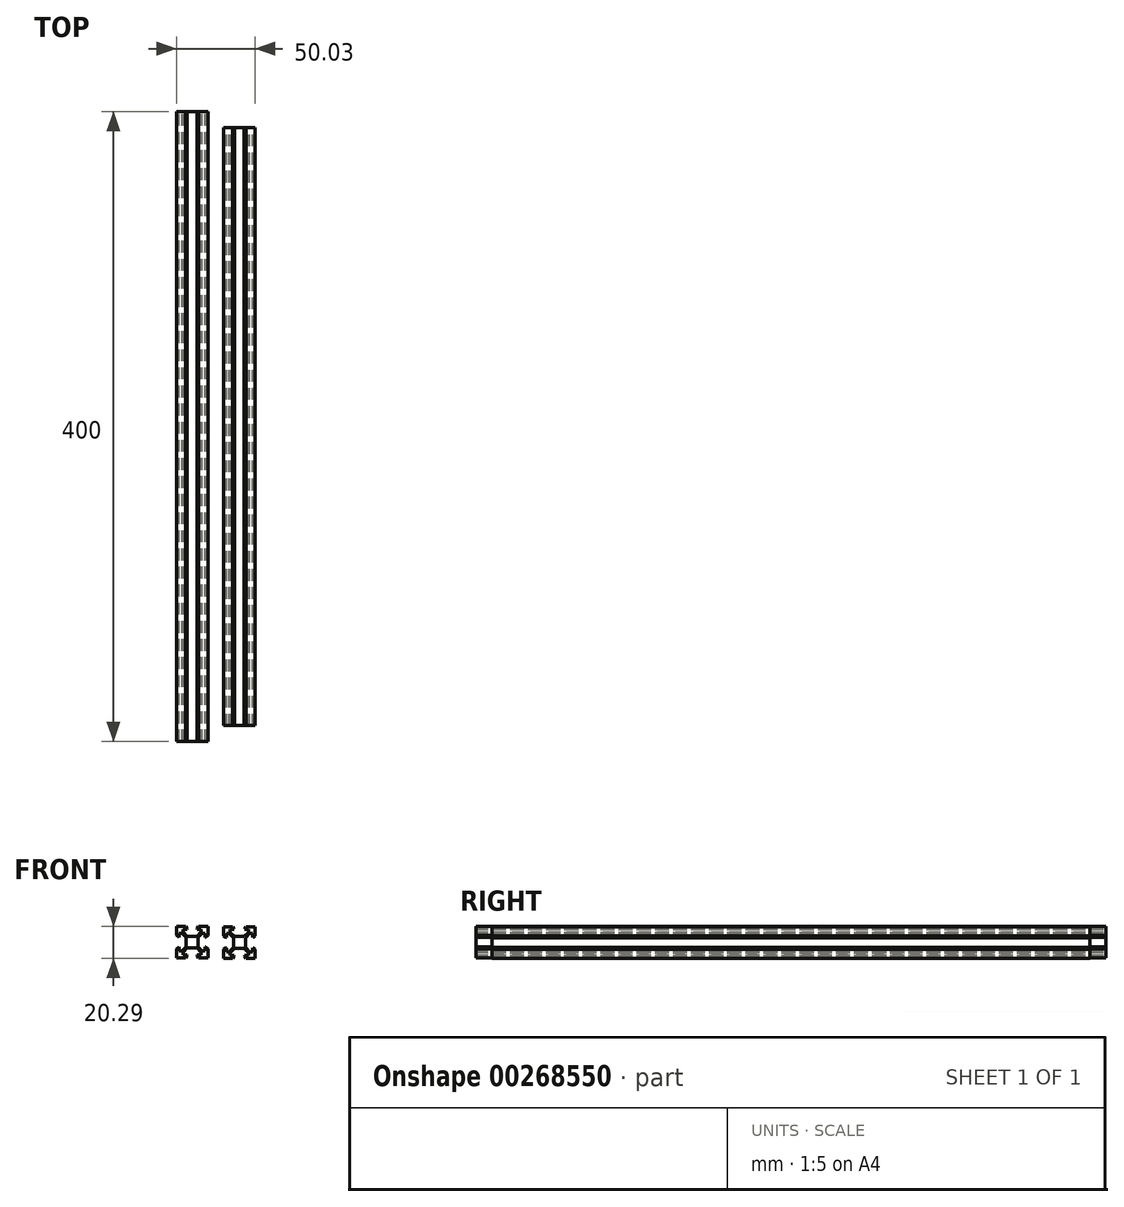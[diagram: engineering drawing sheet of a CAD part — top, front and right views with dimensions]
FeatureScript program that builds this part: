
annotation { "Feature Type Name" : "Feature", "Feature Type Description" : "" }
export const myFeature = defineFeature(function(context is Context, id is Id, definition is map)
    precondition{}
    {
        {
            var Q0;
            Q0=qCreatedBy(makeId("Front.planeOp"),FACE);
            var sketch = newSketch(context, id + "F0", { "sketchPlane" : qUnion([Q0])});
            skLineSegment(sketch, "E0.bottom", {"start": v(10, -10) * mm, "end": v(-10, -10) * mm});
            skLineSegment(sketch, "E0.top", {"start": v(10, 10) * mm, "end": v(-10, 10) * mm});
            skLineSegment(sketch, "E0.left", {"start": v(10, -10) * mm, "end": v(10, 10) * mm});
            skLineSegment(sketch, "E0.right", {"start": v(-10, -10) * mm, "end": v(-10, 10) * mm});
            skPoint(sketch, "E0.middle", {"position": v(0, 0) * mm});
            skLineSegment(sketch, "E1", {"start": v(4.24, 10) * mm, "end": v(3.26, 8.42) * mm});
            skLineSegment(sketch, "E2", {"start": v(3.26, 8.42) * mm, "end": v(3.26, 8.22) * mm});
            skLineSegment(sketch, "E3", {"start": v(3.26, 8.22) * mm, "end": v(5.76, 8.22) * mm});
            skLineSegment(sketch, "E4", {"start": v(5.76, 8.22) * mm, "end": v(5.76, 6.44) * mm});
            skLineSegment(sketch, "E5", {"start": v(5.76, 6.44) * mm, "end": v(3.11, 3.78) * mm});
            skLineSegment(sketch, "E6", {"start": v(3.11, 3.78) * mm, "end": v(0, 3.78) * mm});
            skLineSegment(sketch, "E7", {"start": v(0, 15.87) * mm, "end": v(0, -18.37) * mm, "construction": true});
            skPoint(sketch, "E7.endSnap0", {"position": v(0, -10) * mm});
            skLineSegment(sketch, "E8.MirrorCS", {"start": v(-4.24, 10) * mm, "end": v(-3.26, 8.42) * mm});
            skLineSegment(sketch, "E9.MirrorCS", {"start": v(-3.26, 8.42) * mm, "end": v(-3.26, 8.22) * mm});
            skLineSegment(sketch, "E10.MirrorCS", {"start": v(-3.26, 8.22) * mm, "end": v(-5.76, 8.22) * mm});
            skLineSegment(sketch, "E11.MirrorCS", {"start": v(-5.46, 15.87) * mm, "end": v(-5.46, -18.37) * mm, "construction": true});
            skLineSegment(sketch, "E12.MirrorCS", {"start": v(-5.76, 6.44) * mm, "end": v(-3.11, 3.78) * mm});
            skLineSegment(sketch, "E13.MirrorCS", {"start": v(-3.11, 3.78) * mm, "end": v(0, 3.78) * mm});
            skLineSegment(sketch, "E14.MirrorCS", {"start": v(-5.76, 8.22) * mm, "end": v(-5.76, 6.44) * mm});
            skLineSegment(sketch, "E15.1.0", {"start": v(-3.78, 3.11) * mm, "end": v(-3.78, 0) * mm});
            skLineSegment(sketch, "E15.1.1", {"start": v(-3.78, -3.11) * mm, "end": v(-3.78, 0) * mm});
            skLineSegment(sketch, "E15.1.2", {"start": v(-6.44, -5.76) * mm, "end": v(-3.78, -3.11) * mm});
            skLineSegment(sketch, "E15.1.3", {"start": v(-8.22, 3.26) * mm, "end": v(-8.22, 5.76) * mm});
            skLineSegment(sketch, "E15.1.4", {"start": v(-10, 4.24) * mm, "end": v(-8.42, 3.26) * mm});
            skLineSegment(sketch, "E15.1.5", {"start": v(-8.22, 5.76) * mm, "end": v(-6.44, 5.76) * mm});
            skLineSegment(sketch, "E15.1.6", {"start": v(-10, -4.24) * mm, "end": v(-8.42, -3.26) * mm});
            skLineSegment(sketch, "E15.1.7", {"start": v(-6.44, 5.76) * mm, "end": v(-3.78, 3.11) * mm});
            skLineSegment(sketch, "E15.1.8", {"start": v(-8.22, -5.76) * mm, "end": v(-6.44, -5.76) * mm});
            skLineSegment(sketch, "E15.1.9", {"start": v(-8.22, -3.26) * mm, "end": v(-8.22, -5.76) * mm});
            skLineSegment(sketch, "E15.1.10", {"start": v(-8.42, -3.26) * mm, "end": v(-8.22, -3.26) * mm});
            skLineSegment(sketch, "E15.1.11", {"start": v(-8.42, 3.26) * mm, "end": v(-8.22, 3.26) * mm});
            skLineSegment(sketch, "E15.2.0", {"start": v(-3.11, -3.78) * mm, "end": v(0, -3.78) * mm});
            skLineSegment(sketch, "E15.2.1", {"start": v(3.11, -3.78) * mm, "end": v(0, -3.78) * mm});
            skLineSegment(sketch, "E15.2.2", {"start": v(5.76, -6.44) * mm, "end": v(3.11, -3.78) * mm});
            skLineSegment(sketch, "E15.2.3", {"start": v(-3.26, -8.22) * mm, "end": v(-5.76, -8.22) * mm});
            skLineSegment(sketch, "E15.2.4", {"start": v(-4.24, -10) * mm, "end": v(-3.26, -8.42) * mm});
            skLineSegment(sketch, "E15.2.5", {"start": v(-5.76, -8.22) * mm, "end": v(-5.76, -6.44) * mm});
            skLineSegment(sketch, "E15.2.6", {"start": v(4.24, -10) * mm, "end": v(3.26, -8.42) * mm});
            skLineSegment(sketch, "E15.2.7", {"start": v(-5.76, -6.44) * mm, "end": v(-3.11, -3.78) * mm});
            skLineSegment(sketch, "E15.2.8", {"start": v(5.76, -8.22) * mm, "end": v(5.76, -6.44) * mm});
            skLineSegment(sketch, "E15.2.9", {"start": v(3.26, -8.22) * mm, "end": v(5.76, -8.22) * mm});
            skLineSegment(sketch, "E15.2.10", {"start": v(3.26, -8.42) * mm, "end": v(3.26, -8.22) * mm});
            skLineSegment(sketch, "E15.2.11", {"start": v(-3.26, -8.42) * mm, "end": v(-3.26, -8.22) * mm});
            skLineSegment(sketch, "E15.3.0", {"start": v(3.78, -3.11) * mm, "end": v(3.78, 0) * mm});
            skLineSegment(sketch, "E15.3.1", {"start": v(3.78, 3.11) * mm, "end": v(3.78, 0) * mm});
            skLineSegment(sketch, "E15.3.2", {"start": v(6.44, 5.76) * mm, "end": v(3.78, 3.11) * mm});
            skLineSegment(sketch, "E15.3.3", {"start": v(8.22, -3.26) * mm, "end": v(8.22, -5.76) * mm});
            skLineSegment(sketch, "E15.3.4", {"start": v(10, -4.24) * mm, "end": v(8.42, -3.26) * mm});
            skLineSegment(sketch, "E15.3.5", {"start": v(8.22, -5.76) * mm, "end": v(6.44, -5.76) * mm});
            skLineSegment(sketch, "E15.3.6", {"start": v(10, 4.24) * mm, "end": v(8.42, 3.26) * mm});
            skLineSegment(sketch, "E15.3.7", {"start": v(6.44, -5.76) * mm, "end": v(3.78, -3.11) * mm});
            skLineSegment(sketch, "E15.3.8", {"start": v(8.22, 5.76) * mm, "end": v(6.44, 5.76) * mm});
            skLineSegment(sketch, "E15.3.9", {"start": v(8.22, 3.26) * mm, "end": v(8.22, 5.76) * mm});
            skLineSegment(sketch, "E15.3.10", {"start": v(8.42, 3.26) * mm, "end": v(8.22, 3.26) * mm});
            skLineSegment(sketch, "E15.3.11", {"start": v(8.42, -3.26) * mm, "end": v(8.22, -3.26) * mm});
            skSolve(sketch);
        }
        {
            var Q0;
            {var subQ15=sQuery(id+"F0.wireOp",EDGE,"E1");Q0=makeQuery(id+"F0.imprint","IMPRINT",FACE,{"disambiguationData":[TD([[makeQuery(id+"F0.imprint","IMPRINT",EDGE,{"derivedFrom":subQ15}),1.0]])]});}
            extrude(context, id + "F1", {"entities" : qUnion([Q0]), "endBound" : BoundingType.SYMMETRIC, "depth" : 380 * mm});
        }
        {
            var Q0;
            Q0=makeQuery(id+"F1.opExtrude","SWEPT_BODY",BODY,{"disambiguationData":[OSD([sQuery(id+"F0.wireOp",EDGE,"E0.bottom"),sQuery(id+"F0.wireOp",EDGE,"E0.top"),sQuery(id+"F0.wireOp",EDGE,"E0.left"),sQuery(id+"F0.wireOp",EDGE,"E0.right"),sQuery(id+"F0.wireOp",EDGE,"E1"),sQuery(id+"F0.wireOp",EDGE,"E2"),sQuery(id+"F0.wireOp",EDGE,"E3"),sQuery(id+"F0.wireOp",EDGE,"E4"),sQuery(id+"F0.wireOp",EDGE,"E5"),sQuery(id+"F0.wireOp",EDGE,"E6"),sQuery(id+"F0.wireOp",EDGE,"E8.MirrorCS"),sQuery(id+"F0.wireOp",EDGE,"E9.MirrorCS"),sQuery(id+"F0.wireOp",EDGE,"E10.MirrorCS"),sQuery(id+"F0.wireOp",EDGE,"E12.MirrorCS"),sQuery(id+"F0.wireOp",EDGE,"E13.MirrorCS"),sQuery(id+"F0.wireOp",EDGE,"E14.MirrorCS"),sQuery(id+"F0.wireOp",EDGE,"E15.1.0"),sQuery(id+"F0.wireOp",EDGE,"E15.1.1"),sQuery(id+"F0.wireOp",EDGE,"E15.1.2"),sQuery(id+"F0.wireOp",EDGE,"E15.1.3"),sQuery(id+"F0.wireOp",EDGE,"E15.1.4"),sQuery(id+"F0.wireOp",EDGE,"E15.1.5"),sQuery(id+"F0.wireOp",EDGE,"E15.1.6"),sQuery(id+"F0.wireOp",EDGE,"E15.1.7"),sQuery(id+"F0.wireOp",EDGE,"E15.1.8"),sQuery(id+"F0.wireOp",EDGE,"E15.1.9"),sQuery(id+"F0.wireOp",EDGE,"E15.1.10"),sQuery(id+"F0.wireOp",EDGE,"E15.1.11"),sQuery(id+"F0.wireOp",EDGE,"E15.2.0"),sQuery(id+"F0.wireOp",EDGE,"E15.2.1"),sQuery(id+"F0.wireOp",EDGE,"E15.2.2"),sQuery(id+"F0.wireOp",EDGE,"E15.2.3"),sQuery(id+"F0.wireOp",EDGE,"E15.2.4"),sQuery(id+"F0.wireOp",EDGE,"E15.2.5"),sQuery(id+"F0.wireOp",EDGE,"E15.2.6"),sQuery(id+"F0.wireOp",EDGE,"E15.2.7"),sQuery(id+"F0.wireOp",EDGE,"E15.2.8"),sQuery(id+"F0.wireOp",EDGE,"E15.2.9"),sQuery(id+"F0.wireOp",EDGE,"E15.2.10"),sQuery(id+"F0.wireOp",EDGE,"E15.2.11"),sQuery(id+"F0.wireOp",EDGE,"E15.3.0"),sQuery(id+"F0.wireOp",EDGE,"E15.3.1"),sQuery(id+"F0.wireOp",EDGE,"E15.3.2"),sQuery(id+"F0.wireOp",EDGE,"E15.3.3"),sQuery(id+"F0.wireOp",EDGE,"E15.3.4"),sQuery(id+"F0.wireOp",EDGE,"E15.3.5"),sQuery(id+"F0.wireOp",EDGE,"E15.3.6"),sQuery(id+"F0.wireOp",EDGE,"E15.3.7"),sQuery(id+"F0.wireOp",EDGE,"E15.3.8"),sQuery(id+"F0.wireOp",EDGE,"E15.3.9"),sQuery(id+"F0.wireOp",EDGE,"E15.3.10"),sQuery(id+"F0.wireOp",EDGE,"E15.3.11")])]});
            transform(context, id + "F2", {"entities" : qUnion([Q0]), "transformType" : TransformType.COPY});
        }
        {
            var Q0;
            Q0=makeQuery(id+"F2.opPattern","COPY",BODY,{"derivedFrom":makeQuery(id+"F1.opExtrude","SWEPT_BODY",BODY,{"disambiguationData":[OSD([sQuery(id+"F0.wireOp",EDGE,"E0.bottom"),sQuery(id+"F0.wireOp",EDGE,"E0.top"),sQuery(id+"F0.wireOp",EDGE,"E0.left"),sQuery(id+"F0.wireOp",EDGE,"E0.right"),sQuery(id+"F0.wireOp",EDGE,"E1"),sQuery(id+"F0.wireOp",EDGE,"E2"),sQuery(id+"F0.wireOp",EDGE,"E3"),sQuery(id+"F0.wireOp",EDGE,"E4"),sQuery(id+"F0.wireOp",EDGE,"E5"),sQuery(id+"F0.wireOp",EDGE,"E6"),sQuery(id+"F0.wireOp",EDGE,"E8.MirrorCS"),sQuery(id+"F0.wireOp",EDGE,"E9.MirrorCS"),sQuery(id+"F0.wireOp",EDGE,"E10.MirrorCS"),sQuery(id+"F0.wireOp",EDGE,"E12.MirrorCS"),sQuery(id+"F0.wireOp",EDGE,"E13.MirrorCS"),sQuery(id+"F0.wireOp",EDGE,"E14.MirrorCS"),sQuery(id+"F0.wireOp",EDGE,"E15.1.0"),sQuery(id+"F0.wireOp",EDGE,"E15.1.1"),sQuery(id+"F0.wireOp",EDGE,"E15.1.2"),sQuery(id+"F0.wireOp",EDGE,"E15.1.3"),sQuery(id+"F0.wireOp",EDGE,"E15.1.4"),sQuery(id+"F0.wireOp",EDGE,"E15.1.5"),sQuery(id+"F0.wireOp",EDGE,"E15.1.6"),sQuery(id+"F0.wireOp",EDGE,"E15.1.7"),sQuery(id+"F0.wireOp",EDGE,"E15.1.8"),sQuery(id+"F0.wireOp",EDGE,"E15.1.9"),sQuery(id+"F0.wireOp",EDGE,"E15.1.10"),sQuery(id+"F0.wireOp",EDGE,"E15.1.11"),sQuery(id+"F0.wireOp",EDGE,"E15.2.0"),sQuery(id+"F0.wireOp",EDGE,"E15.2.1"),sQuery(id+"F0.wireOp",EDGE,"E15.2.2"),sQuery(id+"F0.wireOp",EDGE,"E15.2.3"),sQuery(id+"F0.wireOp",EDGE,"E15.2.4"),sQuery(id+"F0.wireOp",EDGE,"E15.2.5"),sQuery(id+"F0.wireOp",EDGE,"E15.2.6"),sQuery(id+"F0.wireOp",EDGE,"E15.2.7"),sQuery(id+"F0.wireOp",EDGE,"E15.2.8"),sQuery(id+"F0.wireOp",EDGE,"E15.2.9"),sQuery(id+"F0.wireOp",EDGE,"E15.2.10"),sQuery(id+"F0.wireOp",EDGE,"E15.2.11"),sQuery(id+"F0.wireOp",EDGE,"E15.3.0"),sQuery(id+"F0.wireOp",EDGE,"E15.3.1"),sQuery(id+"F0.wireOp",EDGE,"E15.3.2"),sQuery(id+"F0.wireOp",EDGE,"E15.3.3"),sQuery(id+"F0.wireOp",EDGE,"E15.3.4"),sQuery(id+"F0.wireOp",EDGE,"E15.3.5"),sQuery(id+"F0.wireOp",EDGE,"E15.3.6"),sQuery(id+"F0.wireOp",EDGE,"E15.3.7"),sQuery(id+"F0.wireOp",EDGE,"E15.3.8"),sQuery(id+"F0.wireOp",EDGE,"E15.3.9"),sQuery(id+"F0.wireOp",EDGE,"E15.3.10"),sQuery(id+"F0.wireOp",EDGE,"E15.3.11")])]}),"instanceName":"1"});
            deleteBodies(context, id + "F3", {"entities" : qUnion([Q0])});
        }
        {
            var Q0;
            Q0=makeQuery(id+"F1.opExtrude","SWEPT_BODY",BODY,{"disambiguationData":[OSD([sQuery(id+"F0.wireOp",EDGE,"E0.bottom"),sQuery(id+"F0.wireOp",EDGE,"E0.top"),sQuery(id+"F0.wireOp",EDGE,"E0.left"),sQuery(id+"F0.wireOp",EDGE,"E0.right"),sQuery(id+"F0.wireOp",EDGE,"E1"),sQuery(id+"F0.wireOp",EDGE,"E2"),sQuery(id+"F0.wireOp",EDGE,"E3"),sQuery(id+"F0.wireOp",EDGE,"E4"),sQuery(id+"F0.wireOp",EDGE,"E5"),sQuery(id+"F0.wireOp",EDGE,"E6"),sQuery(id+"F0.wireOp",EDGE,"E8.MirrorCS"),sQuery(id+"F0.wireOp",EDGE,"E9.MirrorCS"),sQuery(id+"F0.wireOp",EDGE,"E10.MirrorCS"),sQuery(id+"F0.wireOp",EDGE,"E12.MirrorCS"),sQuery(id+"F0.wireOp",EDGE,"E13.MirrorCS"),sQuery(id+"F0.wireOp",EDGE,"E14.MirrorCS"),sQuery(id+"F0.wireOp",EDGE,"E15.1.0"),sQuery(id+"F0.wireOp",EDGE,"E15.1.1"),sQuery(id+"F0.wireOp",EDGE,"E15.1.2"),sQuery(id+"F0.wireOp",EDGE,"E15.1.3"),sQuery(id+"F0.wireOp",EDGE,"E15.1.4"),sQuery(id+"F0.wireOp",EDGE,"E15.1.5"),sQuery(id+"F0.wireOp",EDGE,"E15.1.6"),sQuery(id+"F0.wireOp",EDGE,"E15.1.7"),sQuery(id+"F0.wireOp",EDGE,"E15.1.8"),sQuery(id+"F0.wireOp",EDGE,"E15.1.9"),sQuery(id+"F0.wireOp",EDGE,"E15.1.10"),sQuery(id+"F0.wireOp",EDGE,"E15.1.11"),sQuery(id+"F0.wireOp",EDGE,"E15.2.0"),sQuery(id+"F0.wireOp",EDGE,"E15.2.1"),sQuery(id+"F0.wireOp",EDGE,"E15.2.2"),sQuery(id+"F0.wireOp",EDGE,"E15.2.3"),sQuery(id+"F0.wireOp",EDGE,"E15.2.4"),sQuery(id+"F0.wireOp",EDGE,"E15.2.5"),sQuery(id+"F0.wireOp",EDGE,"E15.2.6"),sQuery(id+"F0.wireOp",EDGE,"E15.2.7"),sQuery(id+"F0.wireOp",EDGE,"E15.2.8"),sQuery(id+"F0.wireOp",EDGE,"E15.2.9"),sQuery(id+"F0.wireOp",EDGE,"E15.2.10"),sQuery(id+"F0.wireOp",EDGE,"E15.2.11"),sQuery(id+"F0.wireOp",EDGE,"E15.3.0"),sQuery(id+"F0.wireOp",EDGE,"E15.3.1"),sQuery(id+"F0.wireOp",EDGE,"E15.3.2"),sQuery(id+"F0.wireOp",EDGE,"E15.3.3"),sQuery(id+"F0.wireOp",EDGE,"E15.3.4"),sQuery(id+"F0.wireOp",EDGE,"E15.3.5"),sQuery(id+"F0.wireOp",EDGE,"E15.3.6"),sQuery(id+"F0.wireOp",EDGE,"E15.3.7"),sQuery(id+"F0.wireOp",EDGE,"E15.3.8"),sQuery(id+"F0.wireOp",EDGE,"E15.3.9"),sQuery(id+"F0.wireOp",EDGE,"E15.3.10"),sQuery(id+"F0.wireOp",EDGE,"E15.3.11")])]});
            transform(context, id + "F4", {"entities" : qUnion([Q0]), "transformType" : TransformType.TRANSLATION_3D, "dx" : 30.3 * mm, "dy" : 0 * mm, "dz" : 0 * mm, "makeCopy" : false});
        }
        {
            var Q0;
            Q0=qCreatedBy(makeId("Front.planeOp"),FACE);
            var sketch = newSketch(context, id + "F5", { "sketchPlane" : qUnion([Q0])});
            skLineSegment(sketch, "E16.bottom", {"start": v(10.27, -9.71) * mm, "end": v(-9.73, -9.71) * mm});
            skLineSegment(sketch, "E16.top", {"start": v(10.27, 10.29) * mm, "end": v(-9.73, 10.29) * mm});
            skLineSegment(sketch, "E16.left", {"start": v(10.27, -9.71) * mm, "end": v(10.27, 10.29) * mm});
            skLineSegment(sketch, "E16.right", {"start": v(-9.73, -9.71) * mm, "end": v(-9.73, 10.29) * mm});
            skPoint(sketch, "E16.middle", {"position": v(0.27, 0.29) * mm});
            skLineSegment(sketch, "E17", {"start": v(4.51, 10.29) * mm, "end": v(3.38, 8.71) * mm});
            skLineSegment(sketch, "E18", {"start": v(3.38, 8.71) * mm, "end": v(3.38, 8.5) * mm});
            skLineSegment(sketch, "E19", {"start": v(3.38, 8.5) * mm, "end": v(5.88, 8.5) * mm});
            skLineSegment(sketch, "E20", {"start": v(5.88, 8.5) * mm, "end": v(5.88, 6.73) * mm});
            skLineSegment(sketch, "E21", {"start": v(5.88, 6.73) * mm, "end": v(3.38, 4.06) * mm});
            skLineSegment(sketch, "E22", {"start": v(3.38, 4.06) * mm, "end": v(0.27, 4.06) * mm});
            skLineSegment(sketch, "E23", {"start": v(0.27, 16.16) * mm, "end": v(0.27, -18.08) * mm, "construction": true});
            skPoint(sketch, "E23.endSnap0", {"position": v(0.27, -9.71) * mm});
            skLineSegment(sketch, "E24.MirrorCS", {"start": v(-3.98, 10.29) * mm, "end": v(-2.84, 8.71) * mm});
            skLineSegment(sketch, "E25.MirrorCS", {"start": v(-2.84, 8.71) * mm, "end": v(-2.84, 8.5) * mm});
            skLineSegment(sketch, "E26.MirrorCS", {"start": v(-2.84, 8.5) * mm, "end": v(-5.34, 8.5) * mm});
            skLineSegment(sketch, "E27.MirrorCS", {"start": v(-5.2, 16.16) * mm, "end": v(-5.2, -18.08) * mm, "construction": true});
            skLineSegment(sketch, "E28.MirrorCS", {"start": v(-5.34, 6.73) * mm, "end": v(-2.84, 4.06) * mm});
            skLineSegment(sketch, "E29.MirrorCS", {"start": v(-2.84, 4.06) * mm, "end": v(0.27, 4.06) * mm});
            skLineSegment(sketch, "E30.MirrorCS", {"start": v(-5.34, 8.5) * mm, "end": v(-5.34, 6.73) * mm});
            skLineSegment(sketch, "E31.1.0", {"start": v(-3.5, 3.4) * mm, "end": v(-3.5, 0.29) * mm});
            skLineSegment(sketch, "E31.1.1", {"start": v(-3.5, -2.82) * mm, "end": v(-3.5, 0.29) * mm});
            skLineSegment(sketch, "E31.1.2", {"start": v(-6.18, -5.32) * mm, "end": v(-3.5, -2.82) * mm});
            skLineSegment(sketch, "E31.1.3", {"start": v(-7.95, 3.4) * mm, "end": v(-7.95, 5.9) * mm});
            skLineSegment(sketch, "E31.1.4", {"start": v(-9.73, 4.53) * mm, "end": v(-8.16, 3.4) * mm});
            skLineSegment(sketch, "E31.1.5", {"start": v(-7.95, 5.9) * mm, "end": v(-6.18, 5.9) * mm});
            skLineSegment(sketch, "E31.1.6", {"start": v(-9.73, -3.96) * mm, "end": v(-8.16, -2.82) * mm});
            skLineSegment(sketch, "E31.1.7", {"start": v(-6.18, 5.9) * mm, "end": v(-3.5, 3.4) * mm});
            skLineSegment(sketch, "E31.1.8", {"start": v(-7.95, -5.32) * mm, "end": v(-6.18, -5.32) * mm});
            skLineSegment(sketch, "E31.1.9", {"start": v(-7.95, -2.82) * mm, "end": v(-7.95, -5.32) * mm});
            skLineSegment(sketch, "E31.1.10", {"start": v(-8.16, -2.82) * mm, "end": v(-7.95, -2.82) * mm});
            skLineSegment(sketch, "E31.1.11", {"start": v(-8.16, 3.4) * mm, "end": v(-7.95, 3.4) * mm});
            skLineSegment(sketch, "E31.2.0", {"start": v(-2.84, -3.5) * mm, "end": v(0.27, -3.5) * mm});
            skLineSegment(sketch, "E31.2.1", {"start": v(3.38, -3.5) * mm, "end": v(0.27, -3.5) * mm});
            skLineSegment(sketch, "E31.2.2", {"start": v(5.88, -6.16) * mm, "end": v(3.38, -3.5) * mm});
            skLineSegment(sketch, "E31.2.3", {"start": v(-2.84, -7.94) * mm, "end": v(-5.34, -7.94) * mm});
            skLineSegment(sketch, "E31.2.4", {"start": v(-3.98, -9.71) * mm, "end": v(-2.84, -8.14) * mm});
            skLineSegment(sketch, "E31.2.5", {"start": v(-5.34, -7.94) * mm, "end": v(-5.34, -6.16) * mm});
            skLineSegment(sketch, "E31.2.6", {"start": v(4.51, -9.71) * mm, "end": v(3.38, -8.14) * mm});
            skLineSegment(sketch, "E31.2.7", {"start": v(-5.34, -6.16) * mm, "end": v(-2.84, -3.5) * mm});
            skLineSegment(sketch, "E31.2.8", {"start": v(5.88, -7.94) * mm, "end": v(5.88, -6.16) * mm});
            skLineSegment(sketch, "E31.2.9", {"start": v(3.38, -7.94) * mm, "end": v(5.88, -7.94) * mm});
            skLineSegment(sketch, "E31.2.10", {"start": v(3.38, -8.14) * mm, "end": v(3.38, -7.94) * mm});
            skLineSegment(sketch, "E31.2.11", {"start": v(-2.84, -8.14) * mm, "end": v(-2.84, -7.94) * mm});
            skLineSegment(sketch, "E31.3.0", {"start": v(4.05, -2.82) * mm, "end": v(4.05, 0.29) * mm});
            skLineSegment(sketch, "E31.3.1", {"start": v(4.05, 3.4) * mm, "end": v(4.05, 0.29) * mm});
            skLineSegment(sketch, "E31.3.2", {"start": v(6.71, 5.9) * mm, "end": v(4.05, 3.4) * mm});
            skLineSegment(sketch, "E31.3.3", {"start": v(8.5, -2.82) * mm, "end": v(8.5, -5.32) * mm});
            skLineSegment(sketch, "E31.3.4", {"start": v(10.27, -3.96) * mm, "end": v(8.7, -2.82) * mm});
            skLineSegment(sketch, "E31.3.5", {"start": v(8.5, -5.32) * mm, "end": v(6.71, -5.32) * mm});
            skLineSegment(sketch, "E31.3.6", {"start": v(10.27, 4.53) * mm, "end": v(8.7, 3.4) * mm});
            skLineSegment(sketch, "E31.3.7", {"start": v(6.71, -5.32) * mm, "end": v(4.05, -2.82) * mm});
            skLineSegment(sketch, "E31.3.8", {"start": v(8.5, 5.9) * mm, "end": v(6.71, 5.9) * mm});
            skLineSegment(sketch, "E31.3.9", {"start": v(8.5, 3.4) * mm, "end": v(8.5, 5.9) * mm});
            skLineSegment(sketch, "E31.3.10", {"start": v(8.7, 3.4) * mm, "end": v(8.5, 3.4) * mm});
            skLineSegment(sketch, "E31.3.11", {"start": v(8.7, -2.82) * mm, "end": v(8.5, -2.82) * mm});
            skSolve(sketch);
        }
        {
            var Q0;
            {var subQ11=sQuery(id+"F5.wireOp",EDGE,"E17");Q0=makeQuery(id+"F5.imprint","IMPRINT",FACE,{"disambiguationData":[TD([[makeQuery(id+"F5.imprint","IMPRINT",EDGE,{"derivedFrom":subQ11}),1.0]])]});}
            extrude(context, id + "F6", {"entities" : qUnion([Q0]), "endBound" : BoundingType.SYMMETRIC, "depth" : 400 * mm});
        }
    });
